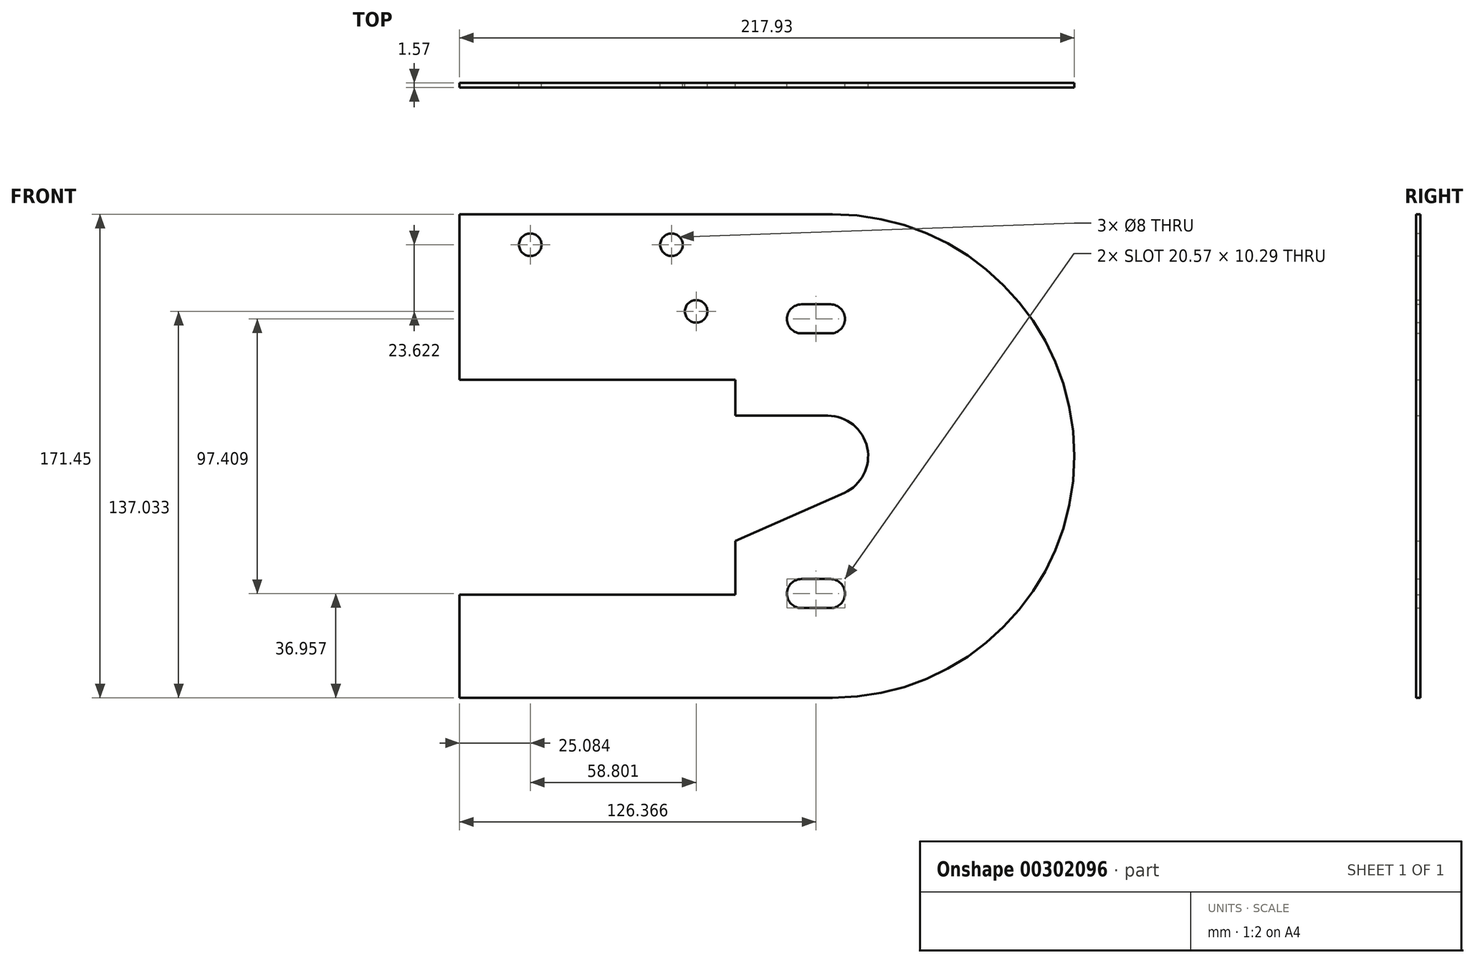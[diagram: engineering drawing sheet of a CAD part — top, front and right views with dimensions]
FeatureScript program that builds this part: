
annotation { "Feature Type Name" : "Feature", "Feature Type Description" : "" }
export const myFeature = defineFeature(function(context is Context, id is Id, definition is map)
    precondition{}
    {
        {
            var Q0;
            Q0=qCreatedBy(makeId("Front.planeOp"),FACE);
            var sketch = newSketch(context, id + "F0", { "sketchPlane" : qUnion([Q0])});
            skLineSegment(sketch, "E0", {"start": v(0, 0) * mm, "end": v(864.64, 0) * mm});
            skLineSegment(sketch, "E1", {"start": v(0, 71.12) * mm, "end": v(138.11, 71.12) * mm});
            skLineSegment(sketch, "E2", {"start": v(138.11, 106.05) * mm, "end": v(0, 106.05) * mm});
            skLineSegment(sketch, "E3", {"start": v(0, 106.05) * mm, "end": v(0, 158.75) * mm});
            skLineSegment(sketch, "E4", {"start": v(0, 158.75) * mm, "end": v(71.5, 200.03) * mm});
            skLineSegment(sketch, "E5", {"start": v(71.5, 200.03) * mm, "end": v(303.21, 200.03) * mm});
            skLineSegment(sketch, "E6", {"start": v(839.24, 323.85) * mm, "end": v(839.24, 171.45) * mm});
            skPoint(sketch, "E7", {"position": v(864.64, 85.73) * mm});
            skArc(sketch, "E8", {"start": v(864.64, 0) * mm, "mid": v(950.36, 85.73) * mm, "end": v(864.64, 171.45) * mm});
            skLineSegment(sketch, "E9", {"start": v(864.64, 171.45) * mm, "end": v(749.53, 171.45) * mm});
            skPoint(sketch, "E10", {"position": v(138.11, 88.58) * mm});
            skPoint(sketch, "E10.positionSnap0", {"position": v(155.58, 88.58) * mm});
            skArc(sketch, "E11", {"start": v(138.11, 71.12) * mm, "mid": v(155.58, 88.58) * mm, "end": v(138.11, 106.04) * mm});
            skLineSegment(sketch, "E12", {"start": v(206.38, 88.58) * mm, "end": v(206.38, 41.91) * mm});
            skLineSegment(sketch, "E13", {"start": v(206.38, 41.91) * mm, "end": v(266.7, 41.91) * mm});
            skLineSegment(sketch, "E14", {"start": v(266.7, 41.91) * mm, "end": v(266.7, 111.76) * mm});
            skLineSegment(sketch, "E15", {"start": v(266.7, 111.76) * mm, "end": v(206.38, 111.76) * mm});
            skLineSegment(sketch, "E16", {"start": v(206.38, 111.76) * mm, "end": v(206.38, 88.58) * mm});
            skLineSegment(sketch, "E17", {"start": v(0, 0) * mm, "end": v(0, 71.12) * mm});
            skPoint(sketch, "E18.orphan", {"position": v(155.58, 106.05) * mm});
            skPoint(sketch, "E19.orphan", {"position": v(155.57, 71.12) * mm});
            skLineSegment(sketch, "E20.bottom", {"start": v(747.67, 36.51) * mm, "end": v(830.22, 36.51) * mm});
            skLineSegment(sketch, "E20.top", {"start": v(747.67, 112.71) * mm, "end": v(830.22, 112.71) * mm});
            skLineSegment(sketch, "E20.left", {"start": v(747.67, 36.51) * mm, "end": v(747.67, 112.71) * mm});
            skLineSegment(sketch, "E20.right", {"start": v(830.22, 36.51) * mm, "end": v(830.22, 55.56) * mm});
            skLineSegment(sketch, "E21", {"start": v(830.22, 100.01) * mm, "end": v(862.98, 100.01) * mm});
            skPoint(sketch, "E22", {"position": v(830.22, 55.56) * mm});
            skPoint(sketch, "E23", {"position": v(862.98, 85.73) * mm});
            skArc(sketch, "E24", {"start": v(868.78, 72.66) * mm, "mid": v(876.96, 88.69) * mm, "end": v(862.98, 100.01) * mm});
            skLineSegment(sketch, "E25", {"start": v(830.22, 55.56) * mm, "end": v(868.78, 72.66) * mm});
            skLineSegment(sketch, "E26.trimOffspring", {"start": v(830.22, 100.01) * mm, "end": v(830.22, 112.71) * mm});
            skLineSegment(sketch, "E27", {"start": v(152.4, 0) * mm, "end": v(152.4, -25.4) * mm});
            skLineSegment(sketch, "E28", {"start": v(152.4, -25.4) * mm, "end": v(864.64, -25.4) * mm});
            skLineSegment(sketch, "E29", {"start": v(864.64, -25.4) * mm, "end": v(864.64, 0) * mm});
            skLineSegment(sketch, "E30", {"start": v(71.5, 200.03) * mm, "end": v(95.54, 212.72) * mm});
            skLineSegment(sketch, "E31", {"start": v(95.54, 212.72) * mm, "end": v(303.21, 212.72) * mm});
            skArc(sketch, "E32.0", {"start": v(868.87, -12.6) * mm, "mid": v(878.37, -11.74) * mm, "end": v(887.74, -9.95) * mm});
            skLineSegment(sketch, "E33", {"start": v(864.64, 184.15) * mm, "end": v(864.64, 171.45) * mm});
            skLineSegment(sketch, "E34", {"start": v(883.57, 169.33) * mm, "end": v(883.6, 182.3) * mm});
            skLineSegment(sketch, "E35", {"start": v(949.83, 95.25) * mm, "end": v(962.6, 95.25) * mm});
            skLineSegment(sketch, "E36", {"start": v(949.83, 76.2) * mm, "end": v(962.6, 76.2) * mm});
            skLineSegment(sketch, "E37", {"start": v(868.87, 0.1) * mm, "end": v(868.87, -12.6) * mm});
            skLineSegment(sketch, "E38", {"start": v(887.68, 3.15) * mm, "end": v(887.74, -9.95) * mm});
            skLineSegment(sketch, "E39", {"start": v(864.64, 85.73) * mm, "end": v(1016.4, 85.73) * mm});
            skLineSegment(sketch, "E40", {"start": v(864.64, 85.72) * mm, "end": v(975.8, 196.9) * mm});
            skLineSegment(sketch, "E41", {"start": v(864.64, 85.73) * mm, "end": v(950.36, 0) * mm});
            skLineSegment(sketch, "E42", {"start": v(918.14, 152.7) * mm, "end": v(927.17, 161.73) * mm});
            skLineSegment(sketch, "E43", {"start": v(931.61, 139.23) * mm, "end": v(940.64, 148.26) * mm});
            skLineSegment(sketch, "E44", {"start": v(931.61, 32.22) * mm, "end": v(940.64, 23.19) * mm});
            skLineSegment(sketch, "E45", {"start": v(918.14, 18.75) * mm, "end": v(927.17, 9.72) * mm});
            skArc(sketch, "E46.trimOffspring", {"start": v(927.17, 9.72) * mm, "mid": v(934.24, 16.13) * mm, "end": v(940.64, 23.19) * mm});
            skArc(sketch, "E47.trimOffspring", {"start": v(962.6, 76.2) * mm, "mid": v(962.95, 80.96) * mm, "end": v(963.06, 85.73) * mm});
            skArc(sketch, "E48.trimOffspring", {"start": v(940.64, 148.26) * mm, "mid": v(934.24, 155.32) * mm, "end": v(927.17, 161.73) * mm});
            skArc(sketch, "E49.trimOffspring", {"start": v(883.6, 182.3) * mm, "mid": v(874.16, 183.69) * mm, "end": v(864.64, 184.15) * mm});
            skLineSegment(sketch, "E50.0", {"start": v(0, 173.41) * mm, "end": v(57.89, 206.84) * mm});
            skLineSegment(sketch, "E51", {"start": v(71.5, 200.03) * mm, "end": v(57.89, 206.84) * mm});
            skLineSegment(sketch, "E52", {"start": v(0, 158.75) * mm, "end": v(0, 173.41) * mm});
            skLineSegment(sketch, "E53", {"start": v(439.73, 200.03) * mm, "end": v(455.23, 200.03) * mm});
            skLineSegment(sketch, "E54.bottom", {"start": v(839.24, 323.85) * mm, "end": v(858.29, 323.85) * mm});
            skLineSegment(sketch, "E54.top", {"start": v(839.24, 273.05) * mm, "end": v(858.29, 273.05) * mm});
            skLineSegment(sketch, "E54.left", {"start": v(839.24, 323.85) * mm, "end": v(839.24, 273.05) * mm});
            skLineSegment(sketch, "E54.right", {"start": v(858.29, 323.85) * mm, "end": v(858.29, 273.05) * mm});
            skLineSegment(sketch, "E55.bottom", {"start": v(839.24, 171.45) * mm, "end": v(858.29, 171.45) * mm});
            skLineSegment(sketch, "E55.top", {"start": v(839.24, 222.25) * mm, "end": v(858.29, 222.25) * mm});
            skLineSegment(sketch, "E55.left", {"start": v(839.24, 171.45) * mm, "end": v(839.24, 222.25) * mm});
            skLineSegment(sketch, "E55.right", {"start": v(858.29, 171.45) * mm, "end": v(858.29, 222.25) * mm});
            skLineSegment(sketch, "E56.bottom", {"start": v(696.36, 112.73) * mm, "end": v(588.41, 112.73) * mm});
            skLineSegment(sketch, "E56.top", {"start": v(696.36, 36.53) * mm, "end": v(588.41, 36.53) * mm});
            skLineSegment(sketch, "E56.left", {"start": v(696.36, 112.73) * mm, "end": v(696.36, 36.53) * mm});
            skLineSegment(sketch, "E56.right", {"start": v(588.41, 112.73) * mm, "end": v(588.41, 36.53) * mm});
            skLineSegment(sketch, "E57", {"start": v(719.92, 106.06) * mm, "end": v(719.92, 47.64) * mm});
            skArc(sketch, "E58", {"start": v(724.05, 106.06) * mm, "mid": v(719.92, 110.19) * mm, "end": v(715.8, 106.06) * mm});
            skCircle(sketch, "E59", {"center": v(719.92, 47.64) * mm, "radius": 4.13 * mm});
            skLineSegment(sketch, "E60", {"start": v(724.05, 106.06) * mm, "end": v(724.05, 47.64) * mm});
            skLineSegment(sketch, "E61", {"start": v(715.8, 106.06) * mm, "end": v(715.8, 47.64) * mm});
            skCircle(sketch, "E62", {"center": v(184.09, 109.82) * mm, "radius": 4.13 * mm});
            skCircle(sketch, "E63", {"center": v(184.09, 65.09) * mm, "radius": 4.13 * mm});
            skCircle(sketch, "E64", {"center": v(227.84, 136.97) * mm, "radius": 4 * mm});
            skLineSegment(sketch, "E65", {"start": v(303.21, 212.72) * mm, "end": v(303.21, 151.77) * mm});
            skLineSegment(sketch, "E66", {"start": v(356.55, 212.72) * mm, "end": v(356.55, 151.77) * mm});
            skLineSegment(sketch, "E67", {"start": v(356.55, 151.77) * mm, "end": v(303.21, 151.77) * mm});
            skPoint(sketch, "E68", {"position": v(595.31, 200.03) * mm});
            skLineSegment(sketch, "E69", {"start": v(595.31, 200.03) * mm, "end": v(839.24, 323.85) * mm});
            skLineSegment(sketch, "E70.trimOffspring", {"start": v(356.55, 200.03) * mm, "end": v(595.31, 200.03) * mm});
            skLineSegment(sketch, "E71.trimOffspring", {"start": v(356.55, 212.72) * mm, "end": v(579.16, 212.72) * mm});
            skLineSegment(sketch, "E72", {"start": v(595.31, 200.03) * mm, "end": v(579.16, 212.72) * mm});
            skCircle(sketch, "E73", {"center": v(757.51, 160.66) * mm, "radius": 4 * mm});
            skCircle(sketch, "E74", {"center": v(816.31, 137.03) * mm, "radius": 4 * mm});
            skCircle(sketch, "E75", {"center": v(807.58, 160.66) * mm, "radius": 4 * mm});
            skCircle(sketch, "E76", {"center": v(853.65, 134.37) * mm, "radius": 5.14 * mm});
            skCircle(sketch, "E77", {"center": v(863.94, 134.37) * mm, "radius": 5.14 * mm});
            skPoint(sketch, "E78", {"position": v(853.65, 36.96) * mm});
            skCircle(sketch, "E79", {"center": v(853.65, 36.96) * mm, "radius": 5.14 * mm});
            skCircle(sketch, "E80", {"center": v(863.94, 36.96) * mm, "radius": 5.14 * mm});
            skLineSegment(sketch, "E81", {"start": v(863.94, 42.1) * mm, "end": v(853.65, 42.1) * mm});
            skLineSegment(sketch, "E82", {"start": v(863.94, 31.81) * mm, "end": v(853.65, 31.81) * mm});
            skLineSegment(sketch, "E83", {"start": v(853.65, 139.5) * mm, "end": v(863.94, 139.5) * mm});
            skLineSegment(sketch, "E84", {"start": v(853.65, 129.22) * mm, "end": v(863.94, 129.22) * mm});
            skCircle(sketch, "E85", {"center": v(31.06, 136.97) * mm, "radius": 4 * mm});
            skCircle(sketch, "E86", {"center": v(424.61, 136.97) * mm, "radius": 4 * mm});
            skCircle(sketch, "E87", {"center": v(621.39, 136.97) * mm, "radius": 4 * mm});
            skCircle(sketch, "E88", {"center": v(244.67, 172.34) * mm, "radius": 4.7 * mm});
            skCircle(sketch, "E89", {"center": v(235.27, 172.34) * mm, "radius": 4.7 * mm});
            skLineSegment(sketch, "E90", {"start": v(244.67, 177.04) * mm, "end": v(235.27, 177.04) * mm});
            skLineSegment(sketch, "E91", {"start": v(244.67, 167.64) * mm, "end": v(235.27, 167.64) * mm});
            skCircle(sketch, "E92", {"center": v(371.8, 190.12) * mm, "radius": 3.43 * mm});
            skLineSegment(sketch, "E93", {"start": v(747.67, 112.71) * mm, "end": v(732.43, 112.71) * mm});
            skLineSegment(sketch, "E94", {"start": v(732.43, 112.71) * mm, "end": v(732.43, 171.45) * mm});
            skLineSegment(sketch, "E95", {"start": v(732.43, 171.45) * mm, "end": v(749.53, 171.45) * mm});
            skLineSegment(sketch, "E96", {"start": v(747.67, 36.51) * mm, "end": v(732.43, 36.51) * mm});
            skLineSegment(sketch, "E97", {"start": v(732.43, 36.51) * mm, "end": v(732.43, 0) * mm});
            skSolve(sketch);
        }
        {
            var Q0;
            Q0=makeQuery(id+"F0.imprint","IMPRINT",FACE,{"disambiguationData":[TD([[makeQuery(id+"F0.imprint","IMPRINT",EDGE,{"derivedFrom":sQuery(id+"F0.wireOp",EDGE,"E20.top")}),1.0]])]});
            var Q1;
            {var subQ5=sQuery(id+"F0.wireOp",EDGE,"E8");var subQ6=makeQuery(id+"F0.imprint","IMPRINT",VERTEX,{"derivedFrom":subQ5});Q1=makeQuery(id+"F0.imprint","IMPRINT",FACE,{"disambiguationData":[TD([[makeQuery(id+"F0.imprint","IMPRINT",EDGE,{"disambiguationData":[TD([[subQ6,1.0]])],"derivedFrom":subQ5}),1.0]])]});}
            var Q2;
            {var subQ5=sQuery(id+"F0.wireOp",EDGE,"E8");var subQ8=makeQuery(id+"F0.imprint","INTERSECT",VERTEX,{"derivedFrom":[subQ5,sQuery(id+"F0.wireOp",EDGE,"E44")]});Q2=makeQuery(id+"F0.imprint","IMPRINT",FACE,{"disambiguationData":[TD([[makeQuery(id+"F0.imprint","IMPRINT",EDGE,{"disambiguationData":[TD([[subQ8,1.0]])],"derivedFrom":subQ5}),1.0]])]});}
            var Q3;
            Q3=makeQuery(id+"F0.imprint","IMPRINT",FACE,{"disambiguationData":[TD([[makeQuery(id+"F0.imprint","IMPRINT",EDGE,{"derivedFrom":sQuery(id+"F0.wireOp",EDGE,"E20.bottom")}),-1.0]])]});
            extrude(context, id + "F1", {"entities" : qUnion([Q0, Q1, Q2, Q3]), "depth" : 1.57 * mm});
        }
    });
